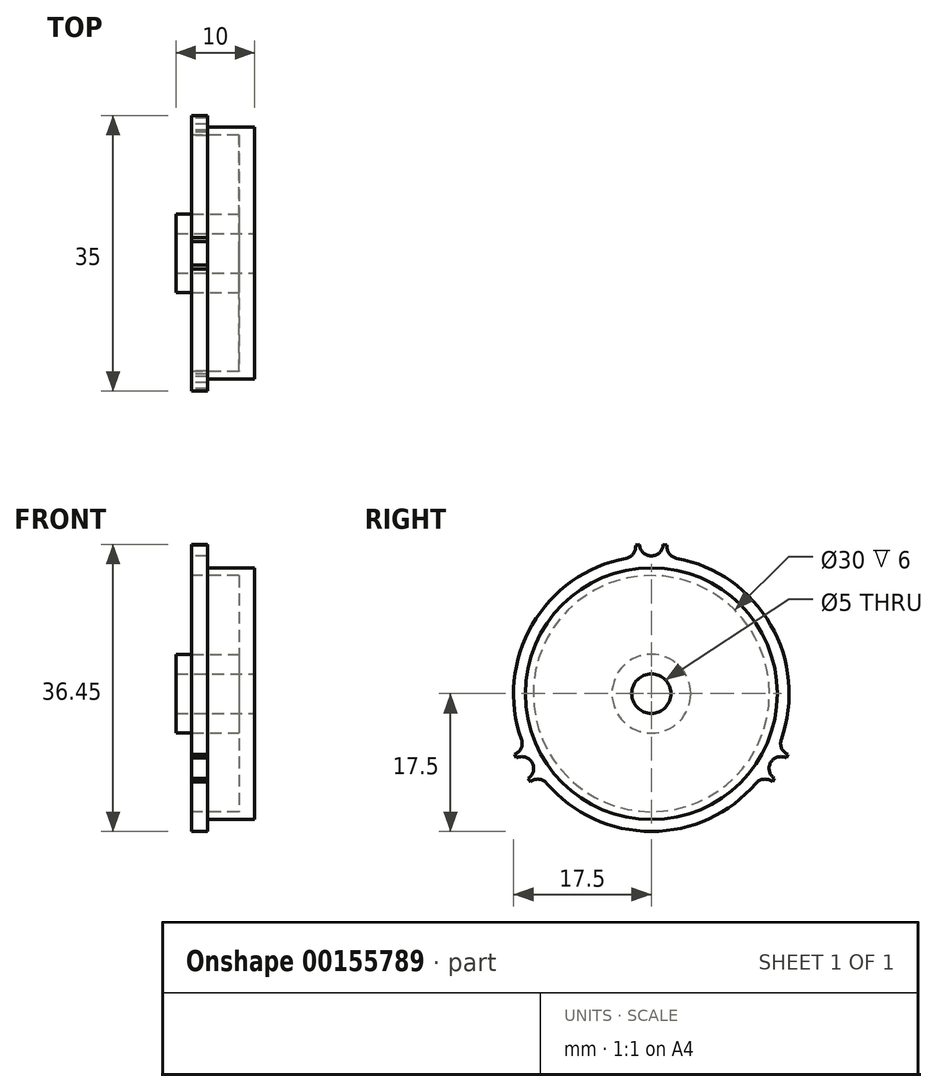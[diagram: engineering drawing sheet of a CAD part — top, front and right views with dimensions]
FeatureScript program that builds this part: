
annotation { "Feature Type Name" : "Feature", "Feature Type Description" : "" }
export const myFeature = defineFeature(function(context is Context, id is Id, definition is map)
    precondition{}
    {
        {
            var Q0;
            Q0=qCreatedBy(makeId("Right.planeOp"),FACE);
            var sketch = newSketch(context, id + "F0", { "sketchPlane" : qUnion([Q0])});
            skLineSegment(sketch, "E0", {"start": v(0, 0) * mm, "end": v(0, 26.77) * mm, "construction": true});
            skLineSegment(sketch, "E1", {"start": v(0, 0) * mm, "end": v(-23.12, -13.35) * mm, "construction": true});
            skLineSegment(sketch, "E2", {"start": v(0, 0) * mm, "end": v(26, -15) * mm, "construction": true});
            skCircle(sketch, "E3", {"center": v(16.45, -9.5) * mm, "radius": 1.5 * mm});
            skCircle(sketch, "E4", {"center": v(0, 19) * mm, "radius": 1.5 * mm});
            skCircle(sketch, "E5", {"center": v(-16.45, -9.5) * mm, "radius": 1.5 * mm});
            skCircle(sketch, "E6", {"center": v(3.49, 18.68) * mm, "radius": 1.5 * mm});
            skCircle(sketch, "E7.MirrorC", {"center": v(-3.49, 18.68) * mm, "radius": 1.5 * mm});
            skCircle(sketch, "E8.MirrorC", {"center": v(-14.43, -12.36) * mm, "radius": 1.5 * mm});
            skCircle(sketch, "E9.MirrorC", {"center": v(-17.92, -6.32) * mm, "radius": 1.5 * mm});
            skCircle(sketch, "E10.MirrorC", {"center": v(17.92, -6.32) * mm, "radius": 1.5 * mm});
            skCircle(sketch, "E11.MirrorC", {"center": v(14.43, -12.36) * mm, "radius": 1.5 * mm});
            skLineSegment(sketch, "E12", {"start": v(-2, 18.9) * mm, "end": v(-1.5, 18.95) * mm});
            skLineSegment(sketch, "E13.MirrorCS", {"start": v(2, 18.9) * mm, "end": v(1.5, 18.95) * mm});
            skLineSegment(sketch, "E14.MirrorCS", {"start": v(-17.36, -7.71) * mm, "end": v(-17.16, -8.18) * mm});
            skLineSegment(sketch, "E15.MirrorCS", {"start": v(-15.36, -11.18) * mm, "end": v(-15.66, -10.77) * mm});
            skLineSegment(sketch, "E16.MirrorCS", {"start": v(15.36, -11.18) * mm, "end": v(15.66, -10.77) * mm});
            skLineSegment(sketch, "E17.MirrorCS", {"start": v(17.36, -7.71) * mm, "end": v(17.16, -8.18) * mm});
            skCircle(sketch, "E18", {"center": v(0, 0) * mm, "radius": 17.5 * mm});
            skSolve(sketch);
        }
        {
            var Q0;
            {var subQ0=sQuery(id+"F0.wireOp",EDGE,"E18");var subQ5=makeQuery(id+"F0.imprint","INTERSECT",VERTEX,{"derivedFrom":[sQuery(id+"F0.wireOp",EDGE,"E6"),subQ0]});Q0=makeQuery(id+"F0.imprint","IMPRINT",FACE,{"disambiguationData":[TD([[makeQuery(id+"F0.imprint","IMPRINT",EDGE,{"disambiguationData":[TD([[subQ5,-1.0]])],"derivedFrom":subQ0}),1.0]])]});}
            var Q1;
            {var subQ0=sQuery(id+"F0.wireOp",EDGE,"E14.MirrorCS");Q1=makeQuery(id+"F0.imprint","IMPRINT",FACE,{"disambiguationData":[TD([[makeQuery(id+"F0.imprint","IMPRINT",EDGE,{"derivedFrom":subQ0}),1.0]])]});}
            var Q2;
            {var subQ0=sQuery(id+"F0.wireOp",EDGE,"E15.MirrorCS");Q2=makeQuery(id+"F0.imprint","IMPRINT",FACE,{"disambiguationData":[TD([[makeQuery(id+"F0.imprint","IMPRINT",EDGE,{"derivedFrom":subQ0}),-1.0]])]});}
            var Q3;
            {var subQ0=sQuery(id+"F0.wireOp",EDGE,"E16.MirrorCS");Q3=makeQuery(id+"F0.imprint","IMPRINT",FACE,{"disambiguationData":[TD([[makeQuery(id+"F0.imprint","IMPRINT",EDGE,{"derivedFrom":subQ0}),1.0]])]});}
            var Q4;
            {var subQ0=sQuery(id+"F0.wireOp",EDGE,"E17.MirrorCS");Q4=makeQuery(id+"F0.imprint","IMPRINT",FACE,{"disambiguationData":[TD([[makeQuery(id+"F0.imprint","IMPRINT",EDGE,{"derivedFrom":subQ0}),-1.0]])]});}
            var Q5;
            {var subQ0=sQuery(id+"F0.wireOp",EDGE,"E13.MirrorCS");Q5=makeQuery(id+"F0.imprint","IMPRINT",FACE,{"disambiguationData":[TD([[makeQuery(id+"F0.imprint","IMPRINT",EDGE,{"derivedFrom":subQ0}),1.0]])]});}
            var Q6;
            {var subQ0=sQuery(id+"F0.wireOp",EDGE,"E12");Q6=makeQuery(id+"F0.imprint","IMPRINT",FACE,{"disambiguationData":[TD([[makeQuery(id+"F0.imprint","IMPRINT",EDGE,{"derivedFrom":subQ0}),-1.0]])]});}
            extrude(context, id + "F1", {"entities" : qUnion([Q0, Q1, Q2, Q3, Q4, Q5, Q6]), "depth" : 8 * mm});
        }
        {
            var Q0;
            Q0=makeQuery(id+"F1.opExtrude","CAP_FACE",FACE,{"disambiguationData":[OSD([sQuery(id+"F0.wireOp",EDGE,"E3"),sQuery(id+"F0.wireOp",EDGE,"E4"),sQuery(id+"F0.wireOp",EDGE,"E5"),sQuery(id+"F0.wireOp",EDGE,"E6"),sQuery(id+"F0.wireOp",EDGE,"E7.MirrorC"),sQuery(id+"F0.wireOp",EDGE,"E8.MirrorC"),sQuery(id+"F0.wireOp",EDGE,"E9.MirrorC"),sQuery(id+"F0.wireOp",EDGE,"E10.MirrorC"),sQuery(id+"F0.wireOp",EDGE,"E11.MirrorC"),sQuery(id+"F0.wireOp",EDGE,"E12"),sQuery(id+"F0.wireOp",EDGE,"E13.MirrorCS"),sQuery(id+"F0.wireOp",EDGE,"E14.MirrorCS"),sQuery(id+"F0.wireOp",EDGE,"E15.MirrorCS"),sQuery(id+"F0.wireOp",EDGE,"E16.MirrorCS"),sQuery(id+"F0.wireOp",EDGE,"E17.MirrorCS"),sQuery(id+"F0.wireOp",EDGE,"E18")])],"isStart":false});
            var sketch = newSketch(context, id + "F2", { "sketchPlane" : qUnion([Q0])});
            skCircle(sketch, "E19", {"center": v(0, 0) * mm, "radius": 19 * mm});
            skCircle(sketch, "E20", {"center": v(0, 0) * mm, "radius": 16 * mm});
            skSolve(sketch);
        }
        {
            var Q0;
            Q0 = qSketchRegion(id + "F2", true);
            extrude(context, id + "F3", {"entities" : qUnion([Q0]), "operationType" : NewBodyOperationType.REMOVE, "oppositeDirection" : true, "depth" : 6 * mm});
        }
        {
            var Q0;
            Q0=makeQuery(id+"F1.opExtrude","CAP_FACE",FACE,{"disambiguationData":[OSD([sQuery(id+"F0.wireOp",EDGE,"E3"),sQuery(id+"F0.wireOp",EDGE,"E4"),sQuery(id+"F0.wireOp",EDGE,"E5"),sQuery(id+"F0.wireOp",EDGE,"E6"),sQuery(id+"F0.wireOp",EDGE,"E7.MirrorC"),sQuery(id+"F0.wireOp",EDGE,"E8.MirrorC"),sQuery(id+"F0.wireOp",EDGE,"E9.MirrorC"),sQuery(id+"F0.wireOp",EDGE,"E10.MirrorC"),sQuery(id+"F0.wireOp",EDGE,"E11.MirrorC"),sQuery(id+"F0.wireOp",EDGE,"E12"),sQuery(id+"F0.wireOp",EDGE,"E13.MirrorCS"),sQuery(id+"F0.wireOp",EDGE,"E14.MirrorCS"),sQuery(id+"F0.wireOp",EDGE,"E15.MirrorCS"),sQuery(id+"F0.wireOp",EDGE,"E16.MirrorCS"),sQuery(id+"F0.wireOp",EDGE,"E17.MirrorCS"),sQuery(id+"F0.wireOp",EDGE,"E18")])],"isStart":true});
            var sketch = newSketch(context, id + "F4", { "sketchPlane" : qUnion([Q0])});
            skCircle(sketch, "E21", {"center": v(0, 0) * mm, "radius": 15 * mm});
            skSolve(sketch);
        }
        {
            var Q0;
            Q0 = qSketchRegion(id + "F4", true);
            extrude(context, id + "F5", {"entities" : qUnion([Q0]), "operationType" : NewBodyOperationType.REMOVE, "oppositeDirection" : true, "depth" : 6 * mm});
        }
        {
            var Q0;
            Q0=makeQuery(id+"F1.opExtrude","CAP_FACE",FACE,{"disambiguationData":[OSD([sQuery(id+"F0.wireOp",EDGE,"E3"),sQuery(id+"F0.wireOp",EDGE,"E4"),sQuery(id+"F0.wireOp",EDGE,"E5"),sQuery(id+"F0.wireOp",EDGE,"E6"),sQuery(id+"F0.wireOp",EDGE,"E7.MirrorC"),sQuery(id+"F0.wireOp",EDGE,"E8.MirrorC"),sQuery(id+"F0.wireOp",EDGE,"E9.MirrorC"),sQuery(id+"F0.wireOp",EDGE,"E10.MirrorC"),sQuery(id+"F0.wireOp",EDGE,"E11.MirrorC"),sQuery(id+"F0.wireOp",EDGE,"E12"),sQuery(id+"F0.wireOp",EDGE,"E13.MirrorCS"),sQuery(id+"F0.wireOp",EDGE,"E14.MirrorCS"),sQuery(id+"F0.wireOp",EDGE,"E15.MirrorCS"),sQuery(id+"F0.wireOp",EDGE,"E16.MirrorCS"),sQuery(id+"F0.wireOp",EDGE,"E17.MirrorCS"),sQuery(id+"F0.wireOp",EDGE,"E18")])],"isStart":false});
            var sketch = newSketch(context, id + "F6", { "sketchPlane" : qUnion([Q0])});
            skCircle(sketch, "E22", {"center": v(0, 0) * mm, "radius": 2.5 * mm});
            skSolve(sketch);
        }
        {
            var Q0;
            Q0 = qSketchRegion(id + "F6", true);
            extrude(context, id + "F7", {"entities" : qUnion([Q0]), "operationType" : NewBodyOperationType.REMOVE, "oppositeDirection" : true, "depth" : 25 * mm});
        }
        {
            var Q0;
            Q0=makeQuery(id+"F5.boolean.opBoolean","COPY",FACE,{"derivedFrom":makeQuery(id+"F5.opExtrude","CAP_FACE",FACE,{"disambiguationData":[OSD([sQuery(id+"F4.wireOp",EDGE,"E21")])],"isStart":false})});
            var sketch = newSketch(context, id + "F8", { "sketchPlane" : qUnion([Q0])});
            skCircle(sketch, "E23", {"center": v(0, 0) * mm, "radius": 5 * mm});
            skCircle(sketch, "E24", {"center": v(0, 0) * mm, "radius": 2.5 * mm});
            skSolve(sketch);
        }
        {
            var Q0;
            Q0 = qSketchRegion(id + "F8", true);
            extrude(context, id + "F9", {"entities" : qUnion([Q0]), "operationType" : NewBodyOperationType.ADD, "depth" : 8 * mm});
        }
    });
